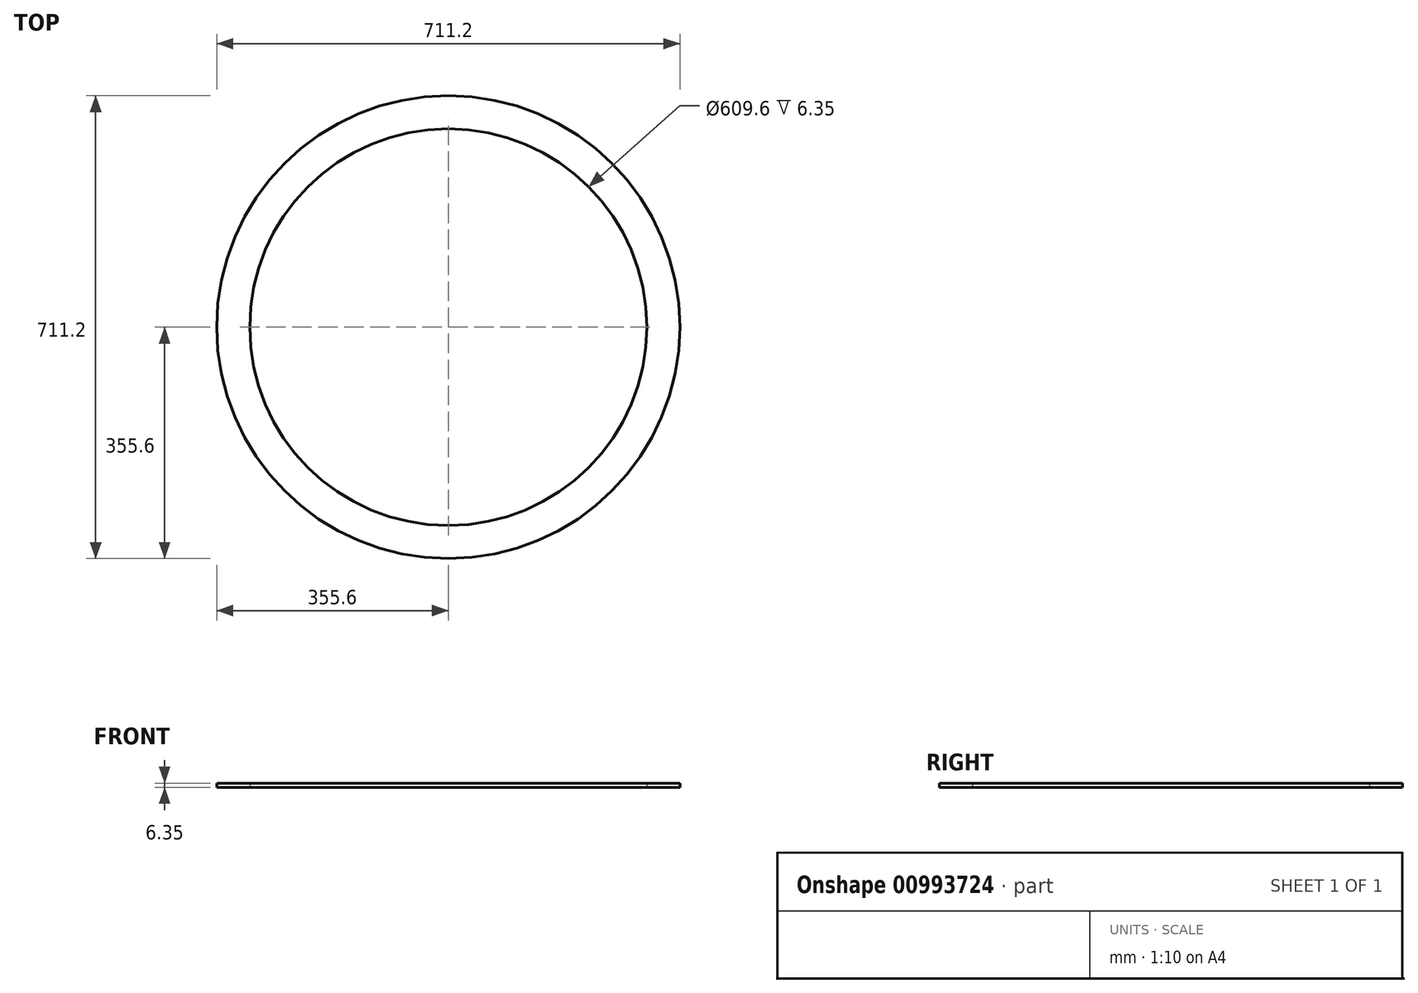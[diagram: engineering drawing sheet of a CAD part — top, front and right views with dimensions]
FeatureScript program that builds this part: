
annotation { "Feature Type Name" : "Feature", "Feature Type Description" : "" }
export const myFeature = defineFeature(function(context is Context, id is Id, definition is map)
    precondition{}
    {
        {
            var Q0;
            Q0=qCreatedBy(makeId("Top.planeOp"),FACE);
            var sketch = newSketch(context, id + "F0", { "sketchPlane" : qUnion([Q0])});
            skCircle(sketch, "E0", {"center": v(0, 0) * mm, "radius": 355.6 * mm});
            skCircle(sketch, "E1", {"center": v(0, 0) * mm, "radius": 304.8 * mm});
            skSolve(sketch);
        }
        {
            var Q0;
            Q0=makeQuery(id+"F0.imprint","IMPRINT",FACE,{"disambiguationData":[TD([[makeQuery(id+"F0.imprint","IMPRINT",EDGE,{"derivedFrom":sQuery(id+"F0.wireOp",EDGE,"E0")}),1.0]])]});
            extrude(context, id + "F1", {"entities" : qUnion([Q0]), "depth" : 6.35 * mm, "offsetDistance" : 25.4 * mm});
        }
    });
